# Revit family: ledwaterproof-e2_l680-10w-4000_543022012600
name_source: partatom
category: Leuchten
revit_build: Autodesk Revit 2016 (Build: 20190508_0715(x64)
units: mm (PartAtom-declared; Revit-internal decimal feet)

## family parameters
Basisbauteil = Fläche
Beim Laden mit Abzugskörper schneiden = Nein
Bemaßung runder Anschluss = Durchmesser verwenden
Gemeinsam genutzt = Nein
Lichtquelle = Nein
Raumberechnungspunkt = Nein
Teiletyp = Normal

## types (1)
- LEDWaterproof-E2 L680-10W-4000 (1 x LED, 1300 lm)
    Approval mark = CE
    Beschreibung = Waterproof luminaire in "sealed-for-life" concept. Quick installation through the easy to open endcap. Up to 50% lower energy consumption compared to traditional TL lighting. Supplied with vandal-proof stainless steel ceiling and suspension clips. Equipped with 3x2.5mm² throughwiring.
    CIE Flux Codes = 42 72 90 94 100
    Control Gear = Electronic ballast
    Height = 56 mm  [stored 0.183727 ft]
    Hersteller = OPPLE
    Lamp Light Flux = 1300 lm
    Lamp count = 1
    Lampe = 1 x LED
    Length = 680 mm
    Luminous efficacy = 128 lm/W
    ModVariant = Nein
    Modell = 543022012600
    Mounting Place = Ceiling
    Mounting Type = Surface mounted
    Number of Poles = 1
    OnlyDefault = Ja
    Power Factor = 1
    Product Name = LEDWaterproof-E2 L680-10W-4000
    Product group = Waterproof EcoMax G2
    ProductGroupID = 347
    Protection Class = Protection class II
    Protection Degree = IP 65
    RLX_Detail_Level = 1
    RlxData = <blob elided: 134113 chars, md5=43091413>
    Scheinlast = 10 VA
    Socket = socket
    Standby Power = 0 W
    System Light Flux = 1300 lm
    System Power = 10 W
    Typenbild = 543022012600.jpg
    Typenkommentare = Product without accessories
    URL = http://relux.com
    VarID = ---
    Voltage = 0 V
    Vorgabe-Ansicht = 1800 mm
    Weight = 0.00 kg
    Width = 60 mm  [stored 0.19685 ft]

note: [stored X ft] marks values corroborated as IEEE doubles in the binary element streams (Revit-internal decimal feet)

## geometry (parser evidence)
native form markers: Blend x4, Sweep x12
no freeform markers — native parametric forms only
